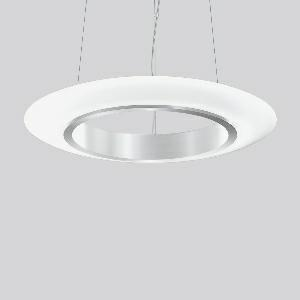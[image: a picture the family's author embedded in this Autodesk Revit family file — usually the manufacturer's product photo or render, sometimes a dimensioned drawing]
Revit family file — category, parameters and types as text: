
# Revit family: ring_of_fire_p_312546_004_1_76_1716
name_source: partatom
category: Lighting Fixtures
units: mm (PartAtom-declared; Revit-internal decimal feet)

## family parameters
Cut with Voids When Loaded = No
Host = Face
Light Source = No
Part Type = Normal
Room Calculation Point = No
Round Connector Dimension = Use Diameter
Shared = No

## types (1)
- RING OF FIRE P (1 x LED Modul 840, 5800 lm, 4000)
    Apparent Load = 71 VA
    CIE Flux Codes = 43 72 90 52 100
    Color Rendering = 80
    Color Temperature = 4000
    Default Elevation = 1800 mm
    Description = Series: RING OF FIRE
A uniquely shaped pendant luminaire with elliptical glass. Supporting ring made of anodised aluminium. Canopy aluminium anodised. Opal glass: mouth-blown, satin finish. Suitable for pendant. 3-point steel cable suspension, steplessly adjustable. Special lengths available on request. 
Colour: anodised aluminium
Diameter: 690 mm
Height: 81 mm
Suspension length: 500-1200 mm
Lamp: LED
Socket: without socket
Colour temperature: 4000K
Colour rendering index (CRI): 80
System power: 71 W
Rated luminous flux: 5800 lm
Luminous efficiency: 82 lm/W
Control gear: Converter, dimmable, DALI
Protection class: I
Type of protection: IP 20
    Height = 81 mm
    Lamp = 1 x LED Modul 840
    Lamp Light Flux = 5800 lm
    Lamp count = 1
    Length = 690 mm
    Lifetime = 50000 h
    Luminous efficacy = 82 lm/W
    Manufacturer = RZB
    ModVariant = No
    Model = 312546.004.1.76
    Mounting Place = Ceiling
    Mounting Type = Pendant
    Number of Poles = 1
    OnlyDefault = Yes
    Power Factor = 1
    Product Name = RING OF FIRE P
    Product group = Pendant luminaires
    ProductGroupID = 902
    Protection Class = Protection class I
    Protection Degree = IP 20
    RLX_Detail_Level = 1
    RLX_Emergency_Light_Flux = 0 lm
    RLX_Emergency_Type = 0
    RLX_Emergency_Type_DB = No
    RlxData = <blob elided: 30425 chars, md5=fa04c609>
    Socket = socket
    Standby Power = 0 W
    System Light Flux = 5800 lm
    System Power = 71 W
    Type Comments = Product without accessories
    Type Image = 311570.004.jpg
    URL = http://relux.com
    VarID = ---
    Voltage = 230 V
    Voltage Range = 220-240 V
    Weight = 0.00 kg
    Width = 0 mm  [stored 0 ft]

note: [stored X ft] marks values corroborated as IEEE doubles in the binary element streams (Revit-internal decimal feet)

## geometry (parser evidence)
native form markers: Blend x4, Sweep x13
no freeform markers — native parametric forms only
